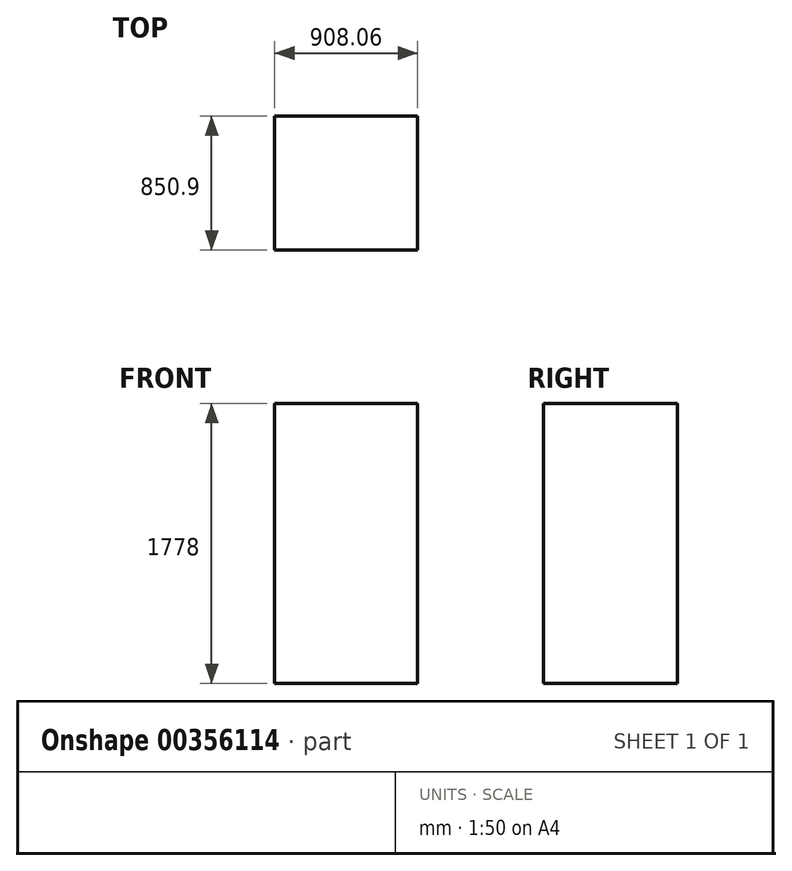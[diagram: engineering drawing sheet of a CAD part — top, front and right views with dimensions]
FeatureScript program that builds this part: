
annotation { "Feature Type Name" : "Feature", "Feature Type Description" : "" }
export const myFeature = defineFeature(function(context is Context, id is Id, definition is map)
    precondition{}
    {
        {
            var Q0;
            Q0=qCreatedBy(makeId("Top.planeOp"),FACE);
            var sketch = newSketch(context, id + "F0", { "sketchPlane" : qUnion([Q0])});
            skLineSegment(sketch, "E0.bottom", {"start": v(-454.03, 425.45) * mm, "end": v(454.03, 425.45) * mm});
            skLineSegment(sketch, "E0.top", {"start": v(-454.03, -425.45) * mm, "end": v(454.03, -425.45) * mm});
            skLineSegment(sketch, "E0.left", {"start": v(-454.03, 425.45) * mm, "end": v(-454.03, -425.45) * mm});
            skLineSegment(sketch, "E0.right", {"start": v(454.03, 425.45) * mm, "end": v(454.03, -425.45) * mm});
            skPoint(sketch, "E0.middle", {"position": v(0, 0) * mm});
            skSolve(sketch);
        }
        {
            var Q0;
            Q0=makeQuery(id+"F0.imprint","IMPRINT",FACE,{"disambiguationData":[TD([[makeQuery(id+"F0.imprint","IMPRINT",EDGE,{"derivedFrom":sQuery(id+"F0.wireOp",EDGE,"E0.bottom")}),-1.0]])]});
            extrude(context, id + "F1", {"entities" : qUnion([Q0]), "depth" : 1778 * mm});
        }
    });
